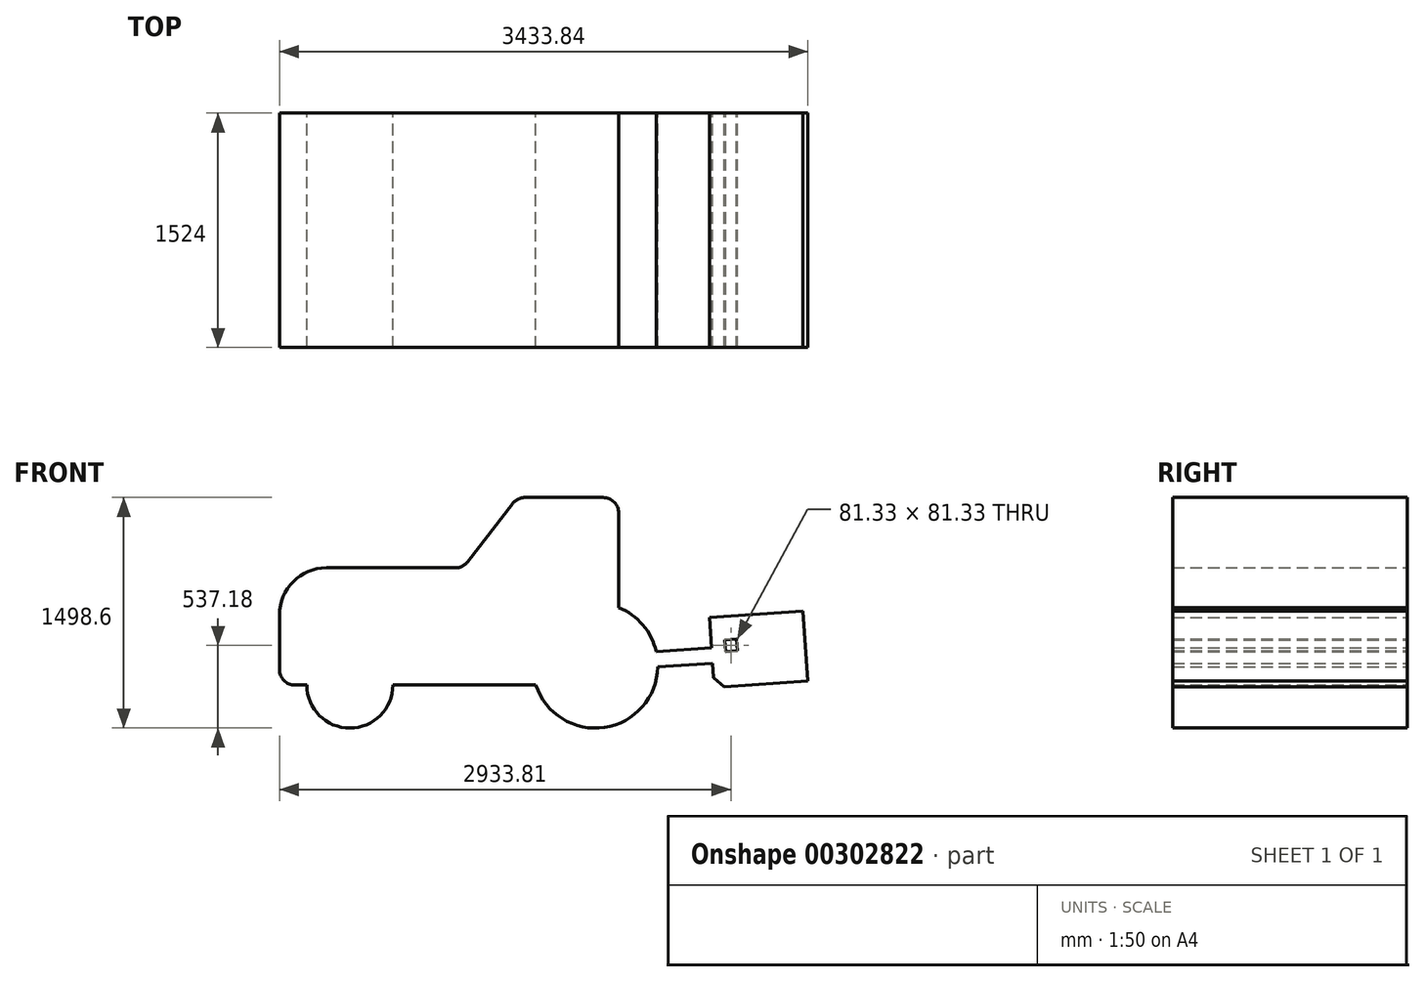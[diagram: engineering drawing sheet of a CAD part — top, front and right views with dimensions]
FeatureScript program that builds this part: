
annotation { "Feature Type Name" : "Feature", "Feature Type Description" : "" }
export const myFeature = defineFeature(function(context is Context, id is Id, definition is map)
    precondition{}
    {
        {
            var Q0;
            Q0=qCreatedBy(makeId("Front.planeOp"),FACE);
            var sketch = newSketch(context, id + "F0", { "sketchPlane" : qUnion([Q0])});
            skCircle(sketch, "E0", {"center": v(0, 406.4) * mm, "radius": 406.4 * mm});
            skLineSegment(sketch, "E1.bottom", {"start": v(741.48, 718.36) * mm, "end": v(1349.6, 760.89) * mm});
            skLineSegment(sketch, "E1.top", {"start": v(836.73, 266.7) * mm, "end": v(1381.5, 304.8) * mm});
            skLineSegment(sketch, "E1.left", {"start": v(741.48, 718.36) * mm, "end": v(768.77, 328.24) * mm});
            skLineSegment(sketch, "E1.right", {"start": v(1349.6, 760.89) * mm, "end": v(1381.5, 304.8) * mm});
            skLineSegment(sketch, "E2", {"start": v(770.94, 323.89) * mm, "end": v(836.73, 266.7) * mm});
            skPoint(sketch, "E3.visualSharp", {"position": v(768.95, 325.62) * mm});
            skArc(sketch, "E3.filletArc", {"start": v(768.77, 328.24) * mm, "mid": v(769.42, 325.85) * mm, "end": v(770.94, 323.89) * mm});
            skLineSegment(sketch, "E4.bottom", {"start": v(840.8, 572.53) * mm, "end": v(916.81, 577.85) * mm});
            skLineSegment(sketch, "E4.top", {"start": v(846.11, 496.52) * mm, "end": v(922.13, 501.83) * mm});
            skLineSegment(sketch, "E4.left", {"start": v(840.8, 572.53) * mm, "end": v(846.11, 496.52) * mm});
            skLineSegment(sketch, "E4.right", {"start": v(916.81, 577.85) * mm, "end": v(922.13, 501.83) * mm});
            skCircle(sketch, "E5", {"center": v(-1595.15, 279.4) * mm, "radius": 279.4 * mm});
            skLineSegment(sketch, "E6.bottom", {"start": v(406.3, 397.05) * mm, "end": v(762.21, 421.94) * mm});
            skLineSegment(sketch, "E6.top", {"start": v(395.9, 498.17) * mm, "end": v(755.12, 523.3) * mm});
            skLineSegment(sketch, "E6.right", {"start": v(762.21, 421.94) * mm, "end": v(755.12, 523.3) * mm});
            skLineSegment(sketch, "E7", {"start": v(-2052.35, 381) * mm, "end": v(-2052.35, 736.6) * mm});
            skLineSegment(sketch, "E8", {"start": v(-1747.55, 1041.4) * mm, "end": v(-909.35, 1041.4) * mm});
            skLineSegment(sketch, "E9", {"start": v(-828.86, 1081) * mm, "end": v(-537.69, 1459) * mm});
            skLineSegment(sketch, "E10", {"start": v(-457.2, 1498.6) * mm, "end": v(50.8, 1498.6) * mm});
            skLineSegment(sketch, "E11", {"start": v(152.4, 1397) * mm, "end": v(152.4, 381) * mm});
            skLineSegment(sketch, "E12", {"start": v(50.8, 279.4) * mm, "end": v(-1950.75, 279.4) * mm});
            skArc(sketch, "E13.filletArc", {"start": v(-1747.55, 1041.4) * mm, "mid": v(-1963.08, 952.13) * mm, "end": v(-2052.35, 736.6) * mm});
            skArc(sketch, "E14.filletArc", {"start": v(-2052.35, 381) * mm, "mid": v(-2022.6, 309.16) * mm, "end": v(-1950.75, 279.4) * mm});
            skArc(sketch, "E15.filletArc", {"start": v(152.4, 1397) * mm, "mid": v(122.64, 1468.84) * mm, "end": v(50.8, 1498.6) * mm});
            skArc(sketch, "E16.filletArc", {"start": v(-457.2, 1498.6) * mm, "mid": v(-502.05, 1488.16) * mm, "end": v(-537.69, 1459) * mm});
            skArc(sketch, "E17.filletArc", {"start": v(-909.35, 1041.4) * mm, "mid": v(-864.5, 1051.84) * mm, "end": v(-828.86, 1081) * mm});
            skArc(sketch, "E18.filletArc", {"start": v(50.8, 279.4) * mm, "mid": v(122.64, 309.16) * mm, "end": v(152.4, 381) * mm});
            skSolve(sketch);
        }
        {
            var Q0;
            Q0 = qSketchRegion(id + "F0", true);
            extrude(context, id + "F1", {"entities" : qUnion([Q0]), "endBound" : BoundingType.SYMMETRIC, "depth" : 1524 * mm});
        }
    });
